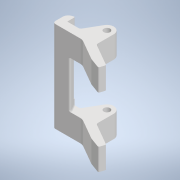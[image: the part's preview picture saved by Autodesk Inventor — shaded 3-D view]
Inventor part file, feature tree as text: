
AUTODESK INVENTOR PART (.ipt)
format: ipt  version: 2022 (Build 260153000, 153)  size: 327,168 bytes
history: native  units: mm
features: reference x14, fillet x8, other x6, extrude x5, sketch x5, projected_geometry x5
ambient origin geometry x8: Origin, YZ Plane, XZ Plane, XY Plane, X Axis, Y Axis, Z Axis, Center Point
bodies: Body1 (feature_tree)
feature tree (43):
  other  "Твердое тело1"
  extrude  "Выдавливание1"  Depth=3.0mm
  extrude  "Выдавливание2"  Depth=12.217305mm
  extrude  "Выдавливание3"  Depth=2.8mm
  fillet  "Сопряжение1"  Radius=0.2mm
  fillet  "Сопряжение2"  Radius=3.0mm
  fillet  "Сопряжение3"  Radius=2.1mm
  fillet  "Сопряжение4"  Radius=6.0mm
  fillet  "Сопряжение5"  [1 undecoded]
  fillet  "Сопряжение6"  Radius=4.5mm
  fillet  "Сопряжение7"  [1 undecoded]
  extrude  "Выдавливание4"  Depth=0.4mm
  fillet  "Сопряжение8"  Radius=3.0mm
  extrude  "Выдавливание5"  TaperAngle=60.0deg  [1 undecoded]
  sketch  "Эскиз1"
  reference  "Ссылка1"
  reference  "Ссылка2"
  reference  "Ссылка4"
  reference  "Ссылка5"
  reference  "Ссылка6"
  reference  "Ссылка7"
  reference  "Ссылка8"
  reference  "Ссылка9"
  reference  "Ссылка10"
  reference  "Ссылка11"
  reference  "Ссылка12"
  sketch  "Эскиз2"
  projected_geometry  "Спроецированная петля1"
  reference  "Ссылка13"
  sketch  "Эскиз3"
  projected_geometry  "Спроецированная петля2"
  sketch  "Эскиз4"
  projected_geometry  "Спроецированная петля3"
  projected_geometry  "Спроецированная петля4"
  reference  "Ссылка14"
  sketch  "Эскиз5"
  projected_geometry  "Спроецированная петля5"
  reference  "Ссылка15"
  other  "<userpath>\Documents\Git\MZCAT_2024\MZCAT_4.iam"
  other  "MZCAT_4.iam"
  other  "base plate:2"
  other  "lidar_krestovina_base:1"
  other  "camera_vision:1"
note: 3 required parameter values undecoded (feature->parameter linkage not recoverable at this tier; creation-order binding heuristic only, values carry confidence <= 0.55)
